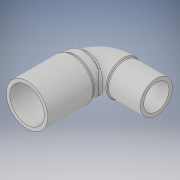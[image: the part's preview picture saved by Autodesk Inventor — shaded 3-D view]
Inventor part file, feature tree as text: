
AUTODESK INVENTOR PART (.ipt)
format: ipt  version: 2019 (Build 230136000, 136)  size: 448,512 bytes
history: native  units: mm
features: sketch x8, fillet x5, extrude x4, sweep x2
ambient origin geometry x8: Origin, YZ Plane, XZ Plane, XY Plane, X Axis, Y Axis, Z Axis, Center Point
bodies: Solid1 (feature_tree)
feature tree (19):
  extrude  "Extrusion1"  Depth=15.0mm
  extrude  "Extrusion2"  Depth=14.0mm
  extrude  "Extrusion3"  Depth=11.0mm
  sweep  "Sweep1"
  sweep  "Sweep2"
  extrude  "Extrusion4"  Depth=5.0mm TaperAngle=0.0deg
  fillet  "Fillet1"  Radius=1.0mm
  fillet  "Fillet2"  Radius=0.4mm
  fillet  "Fillet3"  Radius=0.4mm
  fillet  "Fillet4"  Radius=1.0mm
  fillet  "Fillet5"  Radius=14.0mm
  sketch  "Sketch1"  dims[d0=18.0mm d1=15.0mm]
  sketch  "Sketch2"  dims[d2=20.0mm d3=0.0mm d4=14.0mm]
  sketch  "Sketch3"  dims[d5=11.0mm d6=11.0mm]
  sketch  "Sketch9"  dims[d7=25.0mm d8=0.0mm d9=11.0mm d10=0.0mm]
  sketch  "Sketch10"  dims[d17=18.0mm d30=0.0mm d31=0.0mm]
  sketch  "Sketch11"  dims[d32=0.0mm d33=0.0mm d34=5.0mm d35=0.0mm d36=1.0mm d37=0.4mm d38=0.4mm d39=1.0mm d40=14.0mm]
  sketch  "3D Sketch1"
  sketch  "Sketch12"  dims[d41=1.0mm]
